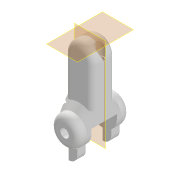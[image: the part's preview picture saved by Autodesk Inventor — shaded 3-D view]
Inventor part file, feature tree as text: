
AUTODESK INVENTOR PART (.ipt)
format: ipt  version: 2020.2 (Build 242310000, 310)  size: 274,944 bytes
history: native  units: mm
features: sketch x9, extrude x6, plane x2, mirror x2, fillet x2, chamfer x1, sweep x1
ambient origin geometry x8: Origin, YZ Plane, XZ Plane, XY Plane, X Axis, Y Axis, Z Axis, Center Point
bodies: Solid1 (feature_tree)
feature tree (23):
  extrude  "base"  Depth=10.0mm
  extrude  "joint"  Depth=20.0mm
  plane  "Work Plane1"
  mirror  "Mirror1"
  chamfer  "Chamfer1"  Distance=8.0mm
  fillet  "Fillet1"  Radius=3.0mm
  extrude  "joint_2"  Depth=5.0mm TaperAngle=0.0deg
  extrude  "lock"  Depth=2.0mm
  mirror  "Mirror2"
  fillet  "Fillet2"  Radius=10.5mm
  sweep  "Sweep2"
  extrude  "Extrusion8"  Depth=3.5mm
  plane  "Work Plane3"
  extrude  "Extrusion9"  Depth=2.5mm
  sketch  "Sketch1"  dims[d0=3.0mm d1=10.0mm]
  sketch  "Sketch2"  dims[d2=20.0mm d3=3.0mm]
  sketch  "Sketch3"  dims[d4=10.0mm d5=8.0mm d6=0.0mm d7=3.0mm]
  sketch  "Sketch9"  dims[d8=10.0mm d9=5.0mm d10=0.0mm]
  sketch  "Sketch10"  dims[d11=2.0mm d12=2.0mm d13=45.0deg d14=2.0mm d15=10.5mm]
  sketch  "Sketch11"  dims[d16=9.0mm d17=0.0mm d21=10.0mm]
  sketch  "Sketch12"  dims[d22=5.25mm d42=3.5mm]
  sketch  "Sketch13"  dims[d43=3.5mm d44=2.5mm]
  sketch  "Sketch14"  dims[d46=25.0mm d47=0.0mm d48=6.0mm d49=3.0mm d50=3.0mm d51=3.0mm d52=0.0mm d53=3.0mm d54=3.0mm d55=7.0mm d57=3.0mm d58=2.0mm d59=2.5mm d60=0.0mm d61=0.0mm d62=4.0mm d63=0.0mm d64=3.5mm d65=3.0mm d66=5.0mm d67=0.0mm]
